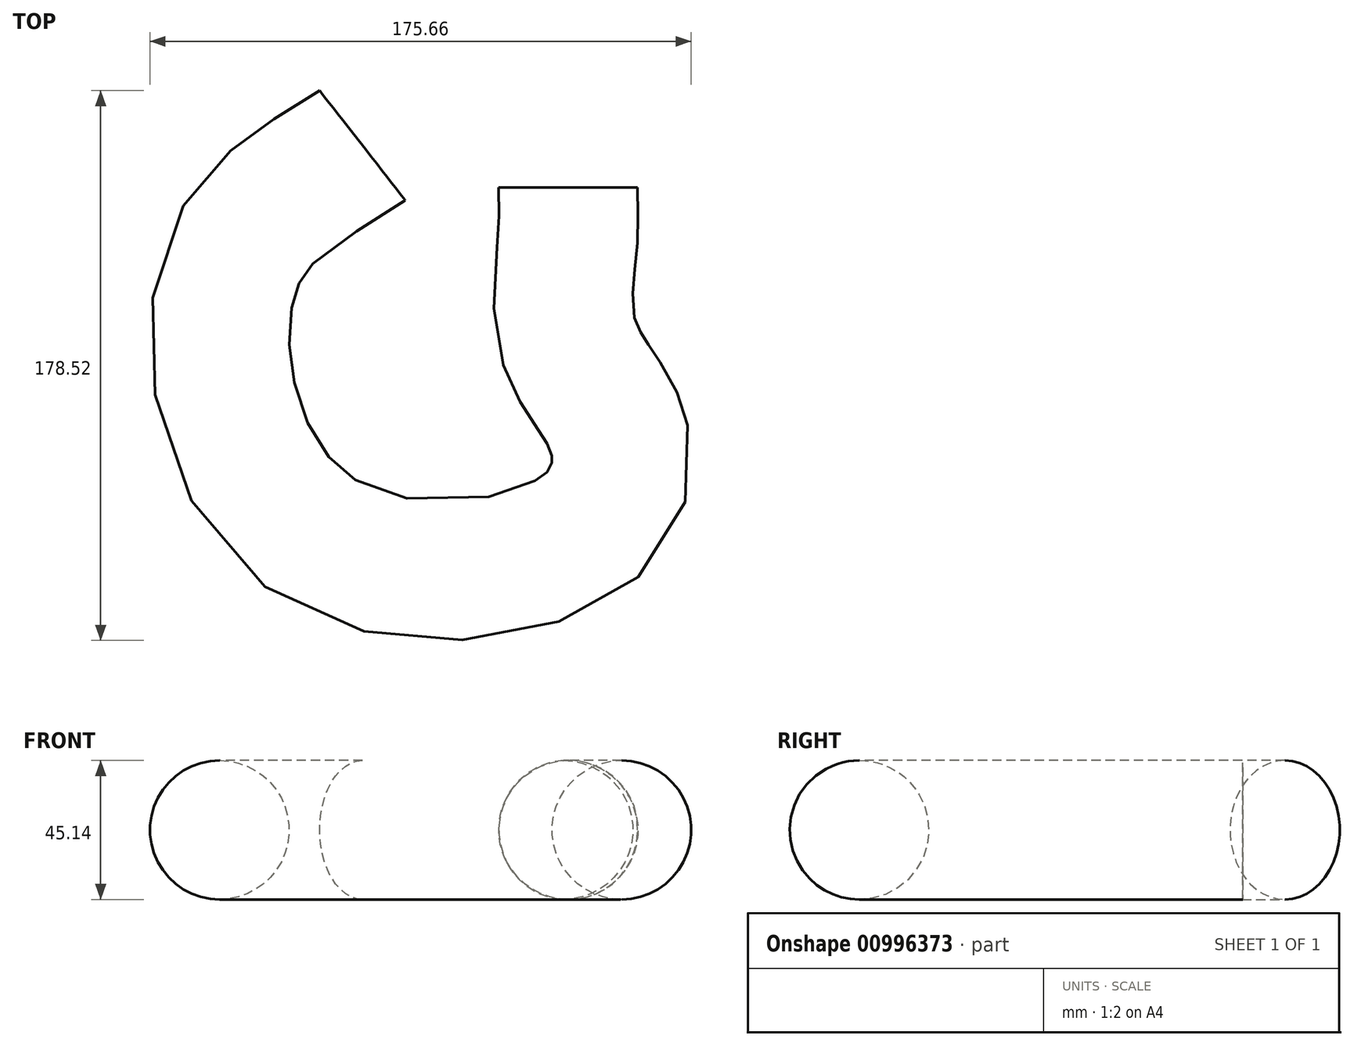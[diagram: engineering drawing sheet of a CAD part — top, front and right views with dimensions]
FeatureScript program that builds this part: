
annotation { "Feature Type Name" : "Feature", "Feature Type Description" : "" }
export const myFeature = defineFeature(function(context is Context, id is Id, definition is map)
    precondition{}
    {
        {
            var Q0;
            Q0=qCreatedBy(makeId("Front.planeOp"),FACE);
            var sketch = newSketch(context, id + "F0", { "sketchPlane" : qUnion([Q0])});
            skCircle(sketch, "E0", {"center": v(0, 0) * mm, "radius": 22.57 * mm});
            skSolve(sketch);
        }
        {
            var Q0;
            Q0=qCreatedBy(makeId("Top.planeOp"),FACE);
            var sketch = newSketch(context, id + "F1", { "sketchPlane" : qUnion([Q0])});
            skFitSpline(sketch, "E1", {"points": [v(0, 0) * mm, v(0, -16.34) * mm, v(0, -49.1) * mm, v(15.4, -77.45) * mm, v(6.63, -110.64) * mm, v(-84.74, -111.66) * mm, v(-107.27, -20.62) * mm, v(-66.73, 13.67) * mm], "startDerivative": vector(0, -412.84) * mm, "endDerivative": vector(196.32, 153.06) * mm});
            skSolve(sketch);
        }
        {
            var Q0;
            {var subQ0=sQuery(id+"F0.wireOp",EDGE,"e23z9cHh-1FaC-apnU-YCDy-RBnjQ4qiCZtx");var subQ1=sQuery(id+"F0.wireOp",EDGE,"E0");var subQ2=makeQuery(id+"F0.imprint","INTERSECT",VERTEX,{"disambiguationData":[OD(0.0)],"derivedFrom":[subQ1,subQ0]});Q0=makeQuery(id+"F0.imprint","IMPRINT",FACE,{"disambiguationData":[TD([[makeQuery(id+"F0.imprint","IMPRINT",EDGE,{"disambiguationData":[TD([[subQ2,-1.0]])],"derivedFrom":subQ1}),1.0]])]});}
            var Q1;
            {var subQ0=sQuery(id+"F0.wireOp",EDGE,"e23z9cHh-1FaC-apnU-YCDy-RBnjQ4qiCZtx");var subQ1=sQuery(id+"F0.wireOp",EDGE,"E0");var subQ2=makeQuery(id+"F0.imprint","INTERSECT",VERTEX,{"disambiguationData":[OD(0.0)],"derivedFrom":[subQ1,subQ0]});Q1=makeQuery(id+"F0.imprint","IMPRINT",FACE,{"disambiguationData":[TD([[makeQuery(id+"F0.imprint","IMPRINT",EDGE,{"disambiguationData":[TD([[subQ2,1.0]])],"derivedFrom":subQ1}),1.0]])]});}
            var Q2;
            Q2=sQuery(id+"F1.wireOp",EDGE,"E1");
            sweep(context, id + "F2", {"profiles" : qUnion([Q0, Q1]), "path" : qUnion([Q2])});
        }
    });
